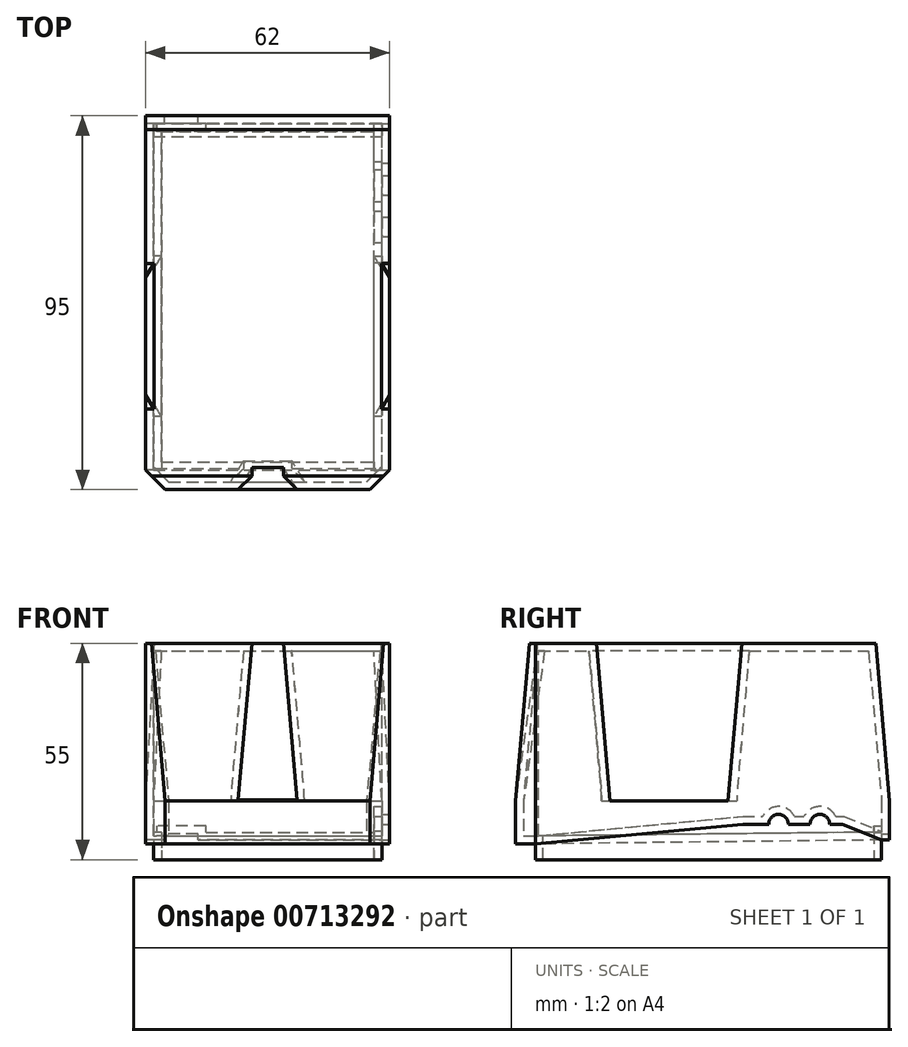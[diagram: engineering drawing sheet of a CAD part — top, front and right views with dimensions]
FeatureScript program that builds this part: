
annotation { "Feature Type Name" : "Feature", "Feature Type Description" : "" }
export const myFeature = defineFeature(function(context is Context, id is Id, definition is map)
    precondition{}
    {
        {
            var Q0;
            Q0=qCreatedBy(makeId("Top.planeOp"),FACE);
            var sketch = newSketch(context, id + "F0", { "sketchPlane" : qUnion([Q0])});
            skLineSegment(sketch, "E0.bottom", {"start": v(-31, -47.5) * mm, "end": v(31, -47.5) * mm});
            skLineSegment(sketch, "E0.top", {"start": v(-31, 47.5) * mm, "end": v(31, 47.5) * mm});
            skLineSegment(sketch, "E0.left", {"start": v(-31, -47.5) * mm, "end": v(-31, 47.5) * mm});
            skLineSegment(sketch, "E0.right", {"start": v(31, -47.5) * mm, "end": v(31, 47.5) * mm});
            skPoint(sketch, "E0.middle", {"position": v(0, 0) * mm});
            skSolve(sketch);
        }
        {
            var Q0;
            Q0=makeQuery(id+"F0.imprint","IMPRINT",FACE,{"disambiguationData":[TD([[makeQuery(id+"F0.imprint","IMPRINT",EDGE,{"derivedFrom":sQuery(id+"F0.wireOp",EDGE,"E0.bottom")}),1.0]])]});
            extrude(context, id + "F1", {"entities" : qUnion([Q0]), "depth" : 55 * mm, "offsetDistance" : 25 * mm});
        }
        {
            var Q0;
            Q0=makeQuery(id+"F1.opExtrude","SWEPT_FACE",FACE,{"disambiguationData":[OSD([sQuery(id+"F0.wireOp",EDGE,"E0.right")])]});
            var sketch = newSketch(context, id + "F2", { "sketchPlane" : qUnion([Q0])});
            skLineSegment(sketch, "E1", {"start": v(-42.5, 4) * mm, "end": v(10.3, 9) * mm});
            skLineSegment(sketch, "E2", {"start": v(10.3, 9) * mm, "end": v(16.8, 9) * mm});
            skArc(sketch, "E3", {"start": v(21.8, 9) * mm, "mid": v(19.3, 11.5) * mm, "end": v(16.8, 9) * mm});
            skLineSegment(sketch, "E4", {"start": v(21.8, 9) * mm, "end": v(27.3, 9) * mm});
            skArc(sketch, "E5", {"start": v(32.3, 9) * mm, "mid": v(29.8, 11.5) * mm, "end": v(27.3, 9) * mm});
            skLineSegment(sketch, "E6", {"start": v(32.3, 9) * mm, "end": v(35.5, 9) * mm});
            skLineSegment(sketch, "E7", {"start": v(35.5, 9) * mm, "end": v(45.5, 5) * mm});
            skLineSegment(sketch, "E8", {"start": v(45.5, 5) * mm, "end": v(47.5, 5) * mm});
            skLineSegment(sketch, "E9", {"start": v(47.5, 5) * mm, "end": v(47.5, 0) * mm});
            skLineSegment(sketch, "E10", {"start": v(47.5, 0) * mm, "end": v(-42.5, 0) * mm});
            skLineSegment(sketch, "E11", {"start": v(-42.5, 0) * mm, "end": v(-42.5, 4) * mm});
            skSolve(sketch);
        }
        {
            var Q0;
            Q0=makeQuery(id+"F2.imprint","IMPRINT",FACE,{"disambiguationData":[TD([[makeQuery(id+"F2.imprint","IMPRINT",EDGE,{"derivedFrom":sQuery(id+"F2.wireOp",EDGE,"E1")}),-1.0]])]});
            extrude(context, id + "F3", {"entities" : qUnion([Q0]), "operationType" : NewBodyOperationType.REMOVE, "oppositeDirection" : true, "depth" : 2 * mm, "offsetDistance" : 25 * mm});
        }
        {
            var Q0;
            Q0=makeQuery(id+"F1.opExtrude","SWEPT_FACE",FACE,{"disambiguationData":[OSD([sQuery(id+"F0.wireOp",EDGE,"E0.top")])]});
            var sketch = newSketch(context, id + "F4", { "sketchPlane" : qUnion([Q0])});
            skLineSegment(sketch, "E12", {"start": v(-29, 5) * mm, "end": v(17.7, 5) * mm});
            skLineSegment(sketch, "E13", {"start": v(17.7, 5) * mm, "end": v(17.7, 6.6) * mm});
            skLineSegment(sketch, "E14", {"start": v(17.7, 6.6) * mm, "end": v(26.2, 6.6) * mm});
            skLineSegment(sketch, "E15", {"start": v(26.2, 6.6) * mm, "end": v(26.2, 5) * mm});
            skLineSegment(sketch, "E16", {"start": v(26.2, 5) * mm, "end": v(31, 5) * mm});
            skLineSegment(sketch, "E17", {"start": v(31, 5) * mm, "end": v(31, 0) * mm});
            skLineSegment(sketch, "E18", {"start": v(31, 0) * mm, "end": v(-29, 0) * mm});
            skLineSegment(sketch, "E19", {"start": v(-29, 0) * mm, "end": v(-29, 5) * mm});
            skSolve(sketch);
        }
        {
            var Q0;
            Q0 = qSketchRegion(id + "F4", true);
            extrude(context, id + "F5", {"entities" : qUnion([Q0]), "operationType" : NewBodyOperationType.REMOVE, "oppositeDirection" : true, "depth" : 2 * mm, "offsetDistance" : 25 * mm});
        }
        {
            var Q0;
            Q0=makeQuery(id+"F1.opExtrude","SWEPT_FACE",FACE,{"disambiguationData":[OSD([sQuery(id+"F0.wireOp",EDGE,"E0.left")])]});
            var sketch = newSketch(context, id + "F6", { "sketchPlane" : qUnion([Q0])});
            skLineSegment(sketch, "E20", {"start": v(-45.5, 5) * mm, "end": v(42.5, 4) * mm});
            skLineSegment(sketch, "E21", {"start": v(42.5, 4) * mm, "end": v(42.5, 0) * mm});
            skLineSegment(sketch, "E22", {"start": v(42.5, 0) * mm, "end": v(-45.5, 0) * mm});
            skLineSegment(sketch, "E23", {"start": v(-45.5, 0) * mm, "end": v(-45.5, 5) * mm});
            skSolve(sketch);
        }
        {
            var Q0;
            Q0 = qSketchRegion(id + "F6", true);
            extrude(context, id + "F7", {"entities" : qUnion([Q0]), "operationType" : NewBodyOperationType.REMOVE, "oppositeDirection" : true, "depth" : 2 * mm, "offsetDistance" : 25 * mm});
        }
        {
            var Q0;
            Q0=makeQuery(id+"F1.opExtrude","SWEPT_FACE",FACE,{"disambiguationData":[OSD([sQuery(id+"F0.wireOp",EDGE,"E0.bottom")])]});
            var sketch = newSketch(context, id + "F8", { "sketchPlane" : qUnion([Q0])});
            skLineSegment(sketch, "E24", {"start": v(-31, 0) * mm, "end": v(-31, 4) * mm});
            skLineSegment(sketch, "E25", {"start": v(-31, 4) * mm, "end": v(31, 4) * mm});
            skLineSegment(sketch, "E26", {"start": v(31, 4) * mm, "end": v(31, 0) * mm});
            skLineSegment(sketch, "E27", {"start": v(31, 0) * mm, "end": v(-31, 0) * mm});
            skSolve(sketch);
        }
        {
            var Q0;
            Q0 = qSketchRegion(id + "F8", true);
            extrude(context, id + "F9", {"entities" : qUnion([Q0]), "operationType" : NewBodyOperationType.REMOVE, "oppositeDirection" : true, "depth" : 5 * mm, "offsetDistance" : 25 * mm});
        }
        {
            var Q0;
            Q0=makeQuery(id+"F1.opExtrude","SWEPT_FACE",FACE,{"disambiguationData":[OSD([sQuery(id+"F0.wireOp",EDGE,"E0.right")])]});
            var sketch = newSketch(context, id + "F10", { "sketchPlane" : qUnion([Q0])});
            skLineSegment(sketch, "E28", {"start": v(-47.5, 55) * mm, "end": v(-44, 55) * mm});
            skLineSegment(sketch, "E29", {"start": v(-44, 55) * mm, "end": v(-47.5, 15) * mm});
            skLineSegment(sketch, "E30", {"start": v(-47.5, 15) * mm, "end": v(-47.5, 55) * mm});
            skLineSegment(sketch, "E31", {"start": v(47.5, 55) * mm, "end": v(47.5, 15) * mm});
            skLineSegment(sketch, "E32", {"start": v(47.5, 15) * mm, "end": v(44, 55) * mm});
            skLineSegment(sketch, "E33", {"start": v(44, 55) * mm, "end": v(47.5, 55) * mm});
            skSolve(sketch);
        }
        {
            var Q0;
            Q0=makeQuery(id+"F10.imprint","IMPRINT",FACE,{"disambiguationData":[TD([[makeQuery(id+"F10.imprint","IMPRINT",EDGE,{"derivedFrom":sQuery(id+"F10.wireOp",EDGE,"E28")}),-1.0]])]});
            var Q1;
            Q1=makeQuery(id+"F10.imprint","IMPRINT",FACE,{"disambiguationData":[TD([[makeQuery(id+"F10.imprint","IMPRINT",EDGE,{"derivedFrom":sQuery(id+"F10.wireOp",EDGE,"E31")}),-1.0]])]});
            extrude(context, id + "F11", {"entities" : qUnion([Q0, Q1]), "operationType" : NewBodyOperationType.REMOVE, "endBound" : BoundingType.THROUGH_ALL, "oppositeDirection" : true, "depth" : 25 * mm, "offsetDistance" : 25 * mm});
        }
        {
            var Q0;
            Q0=makeQuery(id+"F1.opExtrude","SWEPT_FACE",FACE,{"disambiguationData":[OSD([sQuery(id+"F0.wireOp",EDGE,"E0.right")])]});
            var sketch = newSketch(context, id + "F12", { "sketchPlane" : qUnion([Q0])});
            skLineSegment(sketch, "E34", {"start": v(-23.5, 15) * mm, "end": v(6.5, 15) * mm});
            skLineSegment(sketch, "E35", {"start": v(-23.5, 15) * mm, "end": v(-27.5, 60.69) * mm});
            skLineSegment(sketch, "E36", {"start": v(-27.5, 60.69) * mm, "end": v(10.5, 60.69) * mm});
            skLineSegment(sketch, "E37", {"start": v(10.5, 60.69) * mm, "end": v(6.5, 15) * mm});
            skSolve(sketch);
        }
        {
            var Q0;
            Q0 = qSketchRegion(id + "F12", true);
            var Q1;
            Q1=sQuery(id+"F12.wireOp",EDGE,"E34");
            revolve(context, id + "F13", {"operationType" : NewBodyOperationType.REMOVE, "surfaceOperationType" : NewSurfaceOperationType.NEW, "entities" : qUnion([Q0]), "axis" : qUnion([Q1]), "revolveType" : RevolveType.ONE_DIRECTION, "oppositeDirection" : true, "angle" : 3 * degree});
        }
        {
            var Q0;
            Q0=makeQuery(id+"F1.opExtrude","SWEPT_FACE",FACE,{"disambiguationData":[OSD([sQuery(id+"F0.wireOp",EDGE,"E0.left")])]});
            var sketch = newSketch(context, id + "F14", { "sketchPlane" : qUnion([Q0])});
            skLineSegment(sketch, "E38", {"start": v(27.52, 61) * mm, "end": v(23.5, 15) * mm});
            skLineSegment(sketch, "E39", {"start": v(23.5, 15) * mm, "end": v(-6.5, 15) * mm});
            skLineSegment(sketch, "E40", {"start": v(27.52, 61) * mm, "end": v(-10.52, 61) * mm});
            skLineSegment(sketch, "E41", {"start": v(-10.52, 61) * mm, "end": v(-6.5, 15) * mm});
            skSolve(sketch);
        }
        {
            var Q0;
            Q0 = qSketchRegion(id + "F14", true);
            var Q1;
            Q1=sQuery(id+"F14.wireOp",EDGE,"E39");
            revolve(context, id + "F15", {"operationType" : NewBodyOperationType.REMOVE, "surfaceOperationType" : NewSurfaceOperationType.NEW, "entities" : qUnion([Q0]), "axis" : qUnion([Q1]), "revolveType" : RevolveType.ONE_DIRECTION, "angle" : 3 * degree});
        }
        {
            var Q0;
            Q0=makeQuery(id+"F1.opExtrude","SWEPT_EDGE",EDGE,{"disambiguationData":[OSD([sQuery(id+"F0.wireOp",EDGE,"E0.bottom"),sQuery(id+"F0.wireOp",EDGE,"E0.left")])]});
            var Q1;
            Q1=makeQuery(id+"F1.opExtrude","SWEPT_EDGE",EDGE,{"disambiguationData":[OSD([sQuery(id+"F0.wireOp",EDGE,"E0.bottom"),sQuery(id+"F0.wireOp",EDGE,"E0.right")])]});
            chamfer(context, id + "F16", {"entities" : qUnion([Q0, Q1]), "width" : 5 * mm, "tangentPropagation" : true});
        }
        {
            var Q0;
            Q0=makeQuery(id+"F11.boolean.opBoolean","COPY",FACE,{"derivedFrom":makeQuery(id+"F11.opExtrude","SWEPT_FACE",FACE,{"disambiguationData":[OSD([sQuery(id+"F10.wireOp",EDGE,"E29")])]})});
            var sketch = newSketch(context, id + "F17", { "sketchPlane" : qUnion([Q0])});
            skLineSegment(sketch, "E42", {"start": v(-3.48, 56.96) * mm, "end": v(-7.5, 10.96) * mm});
            skLineSegment(sketch, "E43", {"start": v(-7.5, 10.96) * mm, "end": v(7.5, 10.96) * mm});
            skLineSegment(sketch, "E44", {"start": v(7.5, 10.96) * mm, "end": v(3.48, 56.96) * mm});
            skLineSegment(sketch, "E45", {"start": v(3.48, 56.96) * mm, "end": v(-3.48, 56.96) * mm});
            skSolve(sketch);
        }
        {
            var Q0;
            Q0 = qSketchRegion(id + "F17", true);
            var Q1;
            Q1=sQuery(id+"F17.wireOp",EDGE,"E43");
            revolve(context, id + "F18", {"operationType" : NewBodyOperationType.REMOVE, "surfaceOperationType" : NewSurfaceOperationType.NEW, "entities" : qUnion([Q0]), "axis" : qUnion([Q1]), "revolveType" : RevolveType.ONE_DIRECTION, "oppositeDirection" : true, "angle" : 3 * degree});
        }
        {
            var Q0;
            Q0=makeQuery(id+"F1.opExtrude","CAP_FACE",FACE,{"disambiguationData":[OSD([sQuery(id+"F0.wireOp",EDGE,"E0.bottom"),sQuery(id+"F0.wireOp",EDGE,"E0.top"),sQuery(id+"F0.wireOp",EDGE,"E0.left"),sQuery(id+"F0.wireOp",EDGE,"E0.right")])],"isStart":true});
            shell(context, id + "F19", {"entities" : qUnion([Q0]), "thickness" : 2 * mm});
        }
    });
